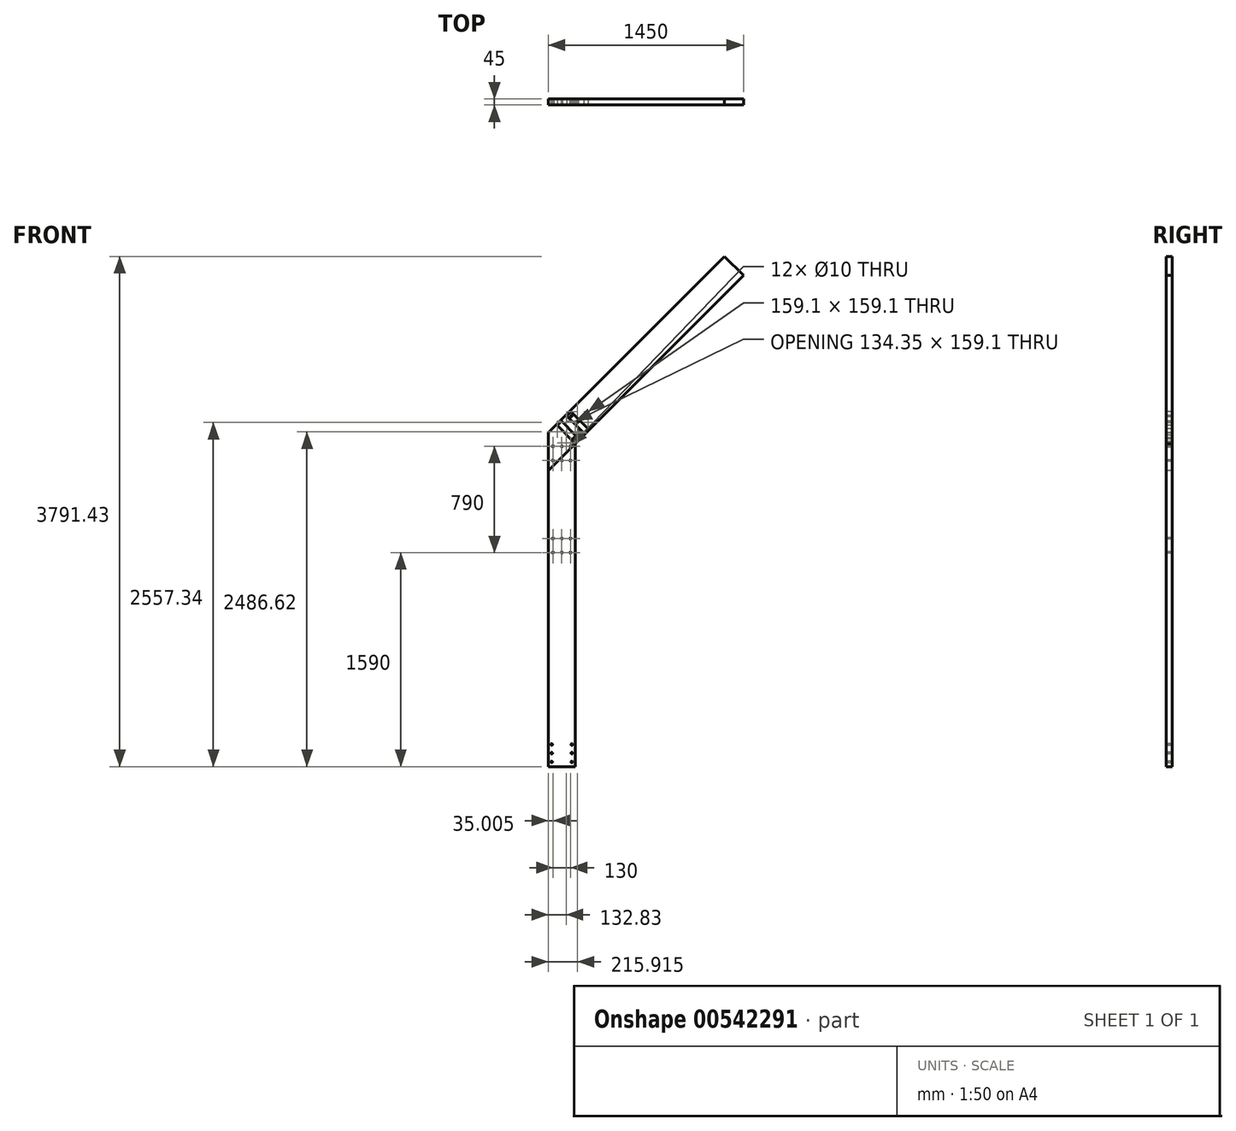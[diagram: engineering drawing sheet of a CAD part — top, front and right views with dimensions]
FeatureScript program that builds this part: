
annotation { "Feature Type Name" : "Feature", "Feature Type Description" : "" }
export const myFeature = defineFeature(function(context is Context, id is Id, definition is map)
    precondition{}
    {
        {
            var Q0;
            Q0=qCreatedBy(makeId("Front.planeOp"),FACE);
            var sketch = newSketch(context, id + "F0", { "sketchPlane" : qUnion([Q0])});
            skLineSegment(sketch, "E0.bottom", {"start": v(-2887.08, 383.58) * mm, "end": v(-5387.08, 383.58) * mm});
            skLineSegment(sketch, "E0.top", {"start": v(-2887.08, -1816.42) * mm, "end": v(-5387.08, -1816.42) * mm});
            skLineSegment(sketch, "E0.left", {"start": v(-2887.08, 383.58) * mm, "end": v(-2887.08, -1816.42) * mm});
            skLineSegment(sketch, "E0.right", {"start": v(-5387.08, 383.58) * mm, "end": v(-5387.08, -1816.42) * mm});
            skLineSegment(sketch, "E1", {"start": v(-5387.08, 383.58) * mm, "end": v(-4137.08, 1633.58) * mm});
            skPoint(sketch, "E1.endSnap0", {"position": v(-4137.08, 383.58) * mm});
            skLineSegment(sketch, "E2", {"start": v(-4137.08, 1633.58) * mm, "end": v(-2887.08, 383.58) * mm});
            skLineSegment(sketch, "E3.0", {"start": v(-4137.08, 1916.43) * mm, "end": v(-2687.08, 466.43) * mm});
            skLineSegment(sketch, "E3.1", {"start": v(-5587.08, 466.43) * mm, "end": v(-4137.08, 1916.43) * mm});
            skLineSegment(sketch, "E3.2", {"start": v(-2687.08, 466.43) * mm, "end": v(-2687.08, -2016.42) * mm});
            skLineSegment(sketch, "E3.3", {"start": v(-2687.08, -2016.42) * mm, "end": v(-5587.08, -2016.42) * mm});
            skLineSegment(sketch, "E3.4", {"start": v(-5587.08, 466.43) * mm, "end": v(-5587.08, -2016.42) * mm});
            skLineSegment(sketch, "E4", {"start": v(-5387.08, -1816.42) * mm, "end": v(-5587.08, -1816.42) * mm});
            skLineSegment(sketch, "E5", {"start": v(-5387.08, -1816.42) * mm, "end": v(-5387.08, -2016.42) * mm});
            skLineSegment(sketch, "E6", {"start": v(-5387.08, 383.58) * mm, "end": v(-5587.08, 466.43) * mm, "construction": true});
            skLineSegment(sketch, "E7", {"start": v(-5387.08, 383.58) * mm, "end": v(-5587.08, 183.58) * mm});
            skLineSegment(sketch, "E8", {"start": v(-5387.08, 383.58) * mm, "end": v(-5387.08, 666.43) * mm});
            skLineSegment(sketch, "E9", {"start": v(-4137.08, 1633.58) * mm, "end": v(-3995.65, 1775) * mm});
            skLineSegment(sketch, "E10", {"start": v(-4137.08, 1633.58) * mm, "end": v(-4278.5, 1775) * mm});
            skLineSegment(sketch, "E11", {"start": v(-5532.08, -2016.42) * mm, "end": v(-5532.08, -1816.42) * mm});
            skLineSegment(sketch, "E12", {"start": v(-5442.08, -1816.42) * mm, "end": v(-5442.08, -2016.42) * mm});
            skLineSegment(sketch, "E13", {"start": v(-2887.08, -1816.42) * mm, "end": v(-2687.08, -1816.42) * mm});
            skLineSegment(sketch, "E14", {"start": v(-2887.08, -1816.42) * mm, "end": v(-2887.08, -2016.42) * mm});
            skLineSegment(sketch, "E15", {"start": v(-2832.08, -1816.42) * mm, "end": v(-2832.08, -2016.42) * mm});
            skLineSegment(sketch, "E16", {"start": v(-2742.08, -1816.42) * mm, "end": v(-2742.08, -2016.42) * mm});
            skLineSegment(sketch, "E17", {"start": v(-4137.08, -1816.42) * mm, "end": v(-4137.08, -2016.42) * mm});
            skLineSegment(sketch, "E18", {"start": v(-4182.08, -1816.42) * mm, "end": v(-4182.08, -2016.42) * mm});
            skLineSegment(sketch, "E19", {"start": v(-4092.08, -1816.42) * mm, "end": v(-4092.08, -2016.42) * mm});
            skLineSegment(sketch, "E20", {"start": v(-4232.08, -1816.42) * mm, "end": v(-4232.08, -2016.42) * mm});
            skLineSegment(sketch, "E21", {"start": v(-4857.08, -1816.42) * mm, "end": v(-4857.08, -2016.42) * mm});
            skLineSegment(sketch, "E22", {"start": v(-4767.08, -1816.42) * mm, "end": v(-4767.08, -2016.42) * mm});
            skLineSegment(sketch, "E23", {"start": v(-4907.08, -1816.42) * mm, "end": v(-4907.08, -2016.42) * mm});
            skLineSegment(sketch, "E24", {"start": v(-4717.08, -1816.42) * mm, "end": v(-4717.08, -2016.42) * mm});
            skLineSegment(sketch, "E25.MirrorCS", {"start": v(-3557.08, -1816.42) * mm, "end": v(-3557.08, -2016.42) * mm});
            skLineSegment(sketch, "E26.MirrorCS", {"start": v(-3507.08, -1816.42) * mm, "end": v(-3507.08, -2016.42) * mm});
            skLineSegment(sketch, "E27.MirrorCS", {"start": v(-3417.08, -1816.42) * mm, "end": v(-3417.08, -2016.42) * mm});
            skLineSegment(sketch, "E28.MirrorCS", {"start": v(-3367.08, -1816.42) * mm, "end": v(-3367.08, -2016.42) * mm});
            skLineSegment(sketch, "E29", {"start": v(-5587.08, -1766.42) * mm, "end": v(-5387.08, -1766.42) * mm});
            skLineSegment(sketch, "E30", {"start": v(-5587.08, -1721.42) * mm, "end": v(-5387.08, -1721.42) * mm});
            skLineSegment(sketch, "E31", {"start": v(-5587.08, -1671.42) * mm, "end": v(-5387.08, -1671.42) * mm});
            skLineSegment(sketch, "E32", {"start": v(-5387.08, 333.58) * mm, "end": v(-5587.08, 333.58) * mm});
            skLineSegment(sketch, "E33", {"start": v(-5587.08, 288.58) * mm, "end": v(-5387.08, 288.58) * mm});
            skLineSegment(sketch, "E34", {"start": v(-5587.08, 238.58) * mm, "end": v(-5387.08, 238.58) * mm});
            skLineSegment(sketch, "E35", {"start": v(-5587.08, -1131.42) * mm, "end": v(-5387.08, -1131.42) * mm});
            skLineSegment(sketch, "E36", {"start": v(-5587.08, -1081.42) * mm, "end": v(-5387.08, -1081.42) * mm});
            skLineSegment(sketch, "E37", {"start": v(-5587.08, -1036.42) * mm, "end": v(-5387.08, -1036.42) * mm});
            skLineSegment(sketch, "E38", {"start": v(-5587.08, -986.42) * mm, "end": v(-5387.08, -986.42) * mm});
            skLineSegment(sketch, "E39", {"start": v(-5587.08, -446.42) * mm, "end": v(-5387.08, -446.42) * mm});
            skLineSegment(sketch, "E40", {"start": v(-5587.08, -396.42) * mm, "end": v(-5387.08, -396.42) * mm});
            skLineSegment(sketch, "E41", {"start": v(-5587.08, -351.42) * mm, "end": v(-5387.08, -351.42) * mm});
            skLineSegment(sketch, "E42", {"start": v(-5587.08, -301.42) * mm, "end": v(-5387.08, -301.42) * mm});
            skLineSegment(sketch, "E43", {"start": v(-5387.08, 383.58) * mm, "end": v(-5587.08, 383.58) * mm});
            skLineSegment(sketch, "E44", {"start": v(-5387.08, 383.58) * mm, "end": v(-5528.5, 525) * mm});
            skLineSegment(sketch, "E45", {"start": v(-5493.14, 560.36) * mm, "end": v(-5351.72, 418.94) * mm});
            skLineSegment(sketch, "E46", {"start": v(-5461.32, 592.18) * mm, "end": v(-5319.9, 450.76) * mm});
            skLineSegment(sketch, "E47", {"start": v(-5425.97, 627.54) * mm, "end": v(-5284.54, 486.11) * mm});
            skLineSegment(sketch, "E48", {"start": v(-4313.85, 1739.65) * mm, "end": v(-4172.43, 1598.23) * mm});
            skLineSegment(sketch, "E49", {"start": v(-4345.67, 1707.83) * mm, "end": v(-4204.25, 1566.4) * mm});
            skLineSegment(sketch, "E50", {"start": v(-4381.03, 1672.47) * mm, "end": v(-4239.6, 1531.05) * mm});
            skLineSegment(sketch, "E51", {"start": v(-4955.03, 1098.47) * mm, "end": v(-4813.61, 957.05) * mm});
            skLineSegment(sketch, "E52", {"start": v(-4919.68, 1133.82) * mm, "end": v(-4778.26, 992.4) * mm});
            skLineSegment(sketch, "E53", {"start": v(-4887.86, 1165.64) * mm, "end": v(-4746.44, 1024.22) * mm});
            skLineSegment(sketch, "E54", {"start": v(-4852.5, 1201) * mm, "end": v(-4711.08, 1059.58) * mm});
            skLineSegment(sketch, "E55", {"start": v(-2882.08, -1816.42) * mm, "end": v(-2882.08, -2016.42) * mm});
            skLineSegment(sketch, "E56", {"start": v(-2692.08, -1816.42) * mm, "end": v(-2692.08, -2016.42) * mm});
            skLineSegment(sketch, "E57", {"start": v(-5582.9, -1816.42) * mm, "end": v(-5582.9, -2016.42) * mm});
            skLineSegment(sketch, "E58", {"start": v(-5392.08, -1816.42) * mm, "end": v(-5392.08, -2016.42) * mm});
            skLineSegment(sketch, "E59.MirrorCS", {"start": v(-4042.08, -1816.42) * mm, "end": v(-4042.08, -2016.42) * mm});
            skLineSegment(sketch, "E60", {"start": v(-3507.08, -2016.42) * mm, "end": v(-3507.08, -2085.64) * mm});
            skLineSegment(sketch, "E61", {"start": v(-5487.08, -1816.42) * mm, "end": v(-5487.08, -2016.42) * mm});
            skLineSegment(sketch, "E62", {"start": v(-4812.08, -2016.42) * mm, "end": v(-4812.08, -1816.42) * mm});
            skLineSegment(sketch, "E63", {"start": v(-5587.08, 363.58) * mm, "end": v(-5387.08, 363.58) * mm, "construction": true});
            skLineSegment(sketch, "E64", {"start": v(-5587.08, 258.58) * mm, "end": v(-5387.08, 258.58) * mm, "construction": true});
            skLineSegment(sketch, "E65.MirrorCS", {"start": v(-5514.35, 539.15) * mm, "end": v(-5372.93, 397.73) * mm, "construction": true});
            skLineSegment(sketch, "E66.MirrorCS", {"start": v(-5440.1, 613.4) * mm, "end": v(-5298.69, 471.97) * mm, "construction": true});
            skCircle(sketch, "E67", {"center": v(-5552.08, 363.58) * mm, "radius": 5 * mm});
            skCircle(sketch, "E68", {"center": v(-5422.08, 363.58) * mm, "radius": 5 * mm});
            skCircle(sketch, "E69", {"center": v(-5487.08, 363.58) * mm, "radius": 5 * mm});
            skCircle(sketch, "E70", {"center": v(-5552.08, 258.58) * mm, "radius": 5 * mm});
            skCircle(sketch, "E71", {"center": v(-5487.08, 258.58) * mm, "radius": 5 * mm});
            skCircle(sketch, "E72", {"center": v(-5422.08, 258.58) * mm, "radius": 5 * mm});
            skLineSegment(sketch, "E73", {"start": v(-5577.08, 383.58) * mm, "end": v(-5577.08, 333.58) * mm});
            skLineSegment(sketch, "E74", {"start": v(-5577.08, 288.58) * mm, "end": v(-5577.08, 238.58) * mm});
            skLineSegment(sketch, "E75", {"start": v(-5397.08, 383.58) * mm, "end": v(-5397.08, 333.58) * mm});
            skLineSegment(sketch, "E76", {"start": v(-5397.08, 288.58) * mm, "end": v(-5397.08, 238.58) * mm});
            skLineSegment(sketch, "E77", {"start": v(-5577.08, 338.58) * mm, "end": v(-5397.08, 338.58) * mm});
            skLineSegment(sketch, "E78", {"start": v(-5577.08, 283.58) * mm, "end": v(-5397.08, 283.58) * mm});
            skPoint(sketch, "E79", {"position": v(-5519.58, 363.58) * mm});
            skLineSegment(sketch, "E80.MirrorCS", {"start": v(-5521.43, 517.93) * mm, "end": v(-5486.07, 553.29) * mm});
            skLineSegment(sketch, "E81.MirrorCS", {"start": v(-5394.15, 390.66) * mm, "end": v(-5358.8, 426.01) * mm});
            skLineSegment(sketch, "E82.MirrorCS", {"start": v(-5489.6, 549.75) * mm, "end": v(-5362.33, 422.47) * mm});
            skCircle(sketch, "E83.MirrorC", {"center": v(-5397.68, 422.47) * mm, "radius": 5 * mm});
            skCircle(sketch, "E84.MirrorC", {"center": v(-5443.64, 468.44) * mm, "radius": 5 * mm});
            skCircle(sketch, "E85.MirrorC", {"center": v(-5489.6, 514.4) * mm, "radius": 5 * mm});
            skLineSegment(sketch, "E86.MirrorCS", {"start": v(-5450.71, 588.65) * mm, "end": v(-5323.44, 461.37) * mm});
            skCircle(sketch, "E87.MirrorC", {"center": v(-5415.36, 588.65) * mm, "radius": 5 * mm});
            skCircle(sketch, "E88.MirrorC", {"center": v(-5369.4, 542.68) * mm, "radius": 5 * mm});
            skCircle(sketch, "E89.MirrorC", {"center": v(-5323.44, 496.72) * mm, "radius": 5 * mm});
            skLineSegment(sketch, "E90.MirrorCS", {"start": v(-5326.97, 457.83) * mm, "end": v(-5291.62, 493.19) * mm});
            skLineSegment(sketch, "E91.MirrorCS", {"start": v(-5454.25, 585.1) * mm, "end": v(-5418.9, 620.46) * mm});
            skLineSegment(sketch, "E92", {"start": v(-4310.32, 1743.19) * mm, "end": v(-4168.9, 1601.76) * mm});
            skLineSegment(sketch, "E93", {"start": v(-4349.2, 1704.3) * mm, "end": v(-4207.79, 1562.87) * mm});
            skLineSegment(sketch, "E94", {"start": v(-4925.33, 1128.17) * mm, "end": v(-4783.91, 986.75) * mm});
            skLineSegment(sketch, "E95", {"start": v(-4882.2, 1171.3) * mm, "end": v(-4740.78, 1029.88) * mm});
            skLineSegment(sketch, "E96", {"start": v(-5587.08, -346.42) * mm, "end": v(-5387.08, -346.42) * mm});
            skLineSegment(sketch, "E97", {"start": v(-5587.08, -401.42) * mm, "end": v(-5387.08, -401.42) * mm});
            skLineSegment(sketch, "E98", {"start": v(-5587.08, -1028.42) * mm, "end": v(-5387.08, -1028.42) * mm});
            skLineSegment(sketch, "E99", {"start": v(-5587.08, -1089.42) * mm, "end": v(-5387.08, -1089.42) * mm});
            skLineSegment(sketch, "E100", {"start": v(-5587.08, -1716.42) * mm, "end": v(-5387.08, -1716.42) * mm});
            skLineSegment(sketch, "E101", {"start": v(-5587.08, -1771.42) * mm, "end": v(-5387.08, -1771.42) * mm});
            skLineSegment(sketch, "E102", {"start": v(-5540.08, -1816.42) * mm, "end": v(-5540.08, -2016.42) * mm});
            skLineSegment(sketch, "E103", {"start": v(-5434.08, -1816.42) * mm, "end": v(-5434.08, -2016.42) * mm});
            skLineSegment(sketch, "E104", {"start": v(-4864.23, -1816.42) * mm, "end": v(-4864.23, -2016.42) * mm});
            skLineSegment(sketch, "E105", {"start": v(-4759.08, -1816.42) * mm, "end": v(-4759.08, -2016.42) * mm});
            skLineSegment(sketch, "E106", {"start": v(-4190.08, -1816.42) * mm, "end": v(-4190.08, -2016.42) * mm});
            skLineSegment(sketch, "E107", {"start": v(-5562.08, -1816.42) * mm, "end": v(-5562.08, -2016.42) * mm, "construction": true});
            skCircle(sketch, "E108", {"center": v(-5562.08, -1851.42) * mm, "radius": 6.17 * mm});
            skCircle(sketch, "E109", {"center": v(-5562.08, -1916.42) * mm, "radius": 6 * mm});
            skCircle(sketch, "E110", {"center": v(-5562.08, -1981.42) * mm, "radius": 6 * mm});
            skCircle(sketch, "E111.MirrorC", {"center": v(-5412.08, -1851.42) * mm, "radius": 6.17 * mm});
            skCircle(sketch, "E112.MirrorC", {"center": v(-5412.08, -1916.42) * mm, "radius": 6 * mm});
            skCircle(sketch, "E113.MirrorC", {"center": v(-5412.08, -1981.42) * mm, "radius": 6 * mm});
            skLineSegment(sketch, "E114", {"start": v(-4137.08, 1633.58) * mm, "end": v(-4137.08, 1916.43) * mm});
            skLineSegment(sketch, "E115.bottom", {"start": v(-5587.08, -2016.42) * mm, "end": v(-5645.08, -2016.42) * mm});
            skLineSegment(sketch, "E115.left", {"start": v(-5587.08, -2016.42) * mm, "end": v(-5587.08, -1971.42) * mm});
            skLineSegment(sketch, "E116.bottom", {"start": v(-5645.08, -2016.42) * mm, "end": v(-4137.08, -2016.42) * mm});
            skLineSegment(sketch, "E116.right", {"start": v(-4137.08, -2016.42) * mm, "end": v(-4137.08, -2029.42) * mm});
            skLineSegment(sketch, "E117", {"start": v(-5587.08, 466.43) * mm, "end": v(-5641.54, 488.99) * mm, "construction": true});
            skLineSegment(sketch, "E118", {"start": v(-5600.08, 471.81) * mm, "end": v(-5587.08, 466.43) * mm});
            skLineSegment(sketch, "E119", {"start": v(-4137.08, 1934.81) * mm, "end": v(-4137.08, 1916.43) * mm});
            skLineSegment(sketch, "E120", {"start": v(-4354.86, 1780.66) * mm, "end": v(-4137.08, 1998.45) * mm});
            skLineSegment(sketch, "E121", {"start": v(-4137.08, 1998.45) * mm, "end": v(-4137.08, 2030.98) * mm});
            skLineSegment(sketch, "E122", {"start": v(-4137.08, 1916.43) * mm, "end": v(-4137.08, 2145.54) * mm, "construction": true});
            skLineSegment(sketch, "E123", {"start": v(-5587.08, -321.42) * mm, "end": v(-5387.08, -321.42) * mm, "construction": true});
            skLineSegment(sketch, "E124", {"start": v(-5587.08, -426.42) * mm, "end": v(-5387.08, -426.42) * mm, "construction": true});
            skCircle(sketch, "E125", {"center": v(-5552.08, -321.42) * mm, "radius": 5 * mm});
            skCircle(sketch, "E126", {"center": v(-5487.08, -321.42) * mm, "radius": 5 * mm});
            skCircle(sketch, "E127", {"center": v(-5422.08, -321.42) * mm, "radius": 5 * mm});
            skLineSegment(sketch, "E128", {"start": v(-5587.08, -373.92) * mm, "end": v(-5387.08, -373.92) * mm, "construction": true});
            skCircle(sketch, "E129.MirrorC", {"center": v(-5552.08, -426.42) * mm, "radius": 5 * mm});
            skCircle(sketch, "E130.MirrorC", {"center": v(-5487.08, -426.42) * mm, "radius": 5 * mm});
            skCircle(sketch, "E131.MirrorC", {"center": v(-5422.08, -426.42) * mm, "radius": 5 * mm});
            skLineSegment(sketch, "E132", {"start": v(-2887.08, 383.58) * mm, "end": v(-2687.08, 183.58) * mm});
            skLineSegment(sketch, "E133", {"start": v(-2887.08, 383.58) * mm, "end": v(-2887.08, 666.43) * mm});
            skSolve(sketch);
        }
        {
            var Q0;
            {var subQ0=sQuery(id+"F0.wireOp",EDGE,"E31");Q0=makeQuery(id+"F0.imprint","IMPRINT",FACE,{"disambiguationData":[TD([[makeQuery(id+"F0.imprint","IMPRINT",EDGE,{"derivedFrom":subQ0}),1.0]])]});}
            var Q1;
            {var subQ0=sQuery(id+"F0.wireOp",EDGE,"E31");Q1=makeQuery(id+"F0.imprint","IMPRINT",FACE,{"disambiguationData":[TD([[makeQuery(id+"F0.imprint","IMPRINT",EDGE,{"derivedFrom":subQ0}),-1.0]])]});}
            var Q2;
            {var subQ0=sQuery(id+"F0.wireOp",EDGE,"E30");Q2=makeQuery(id+"F0.imprint","IMPRINT",FACE,{"disambiguationData":[TD([[makeQuery(id+"F0.imprint","IMPRINT",EDGE,{"derivedFrom":subQ0}),1.0]])]});}
            var Q3;
            {var subQ0=sQuery(id+"F0.wireOp",EDGE,"E29");Q3=makeQuery(id+"F0.imprint","IMPRINT",FACE,{"disambiguationData":[TD([[makeQuery(id+"F0.imprint","IMPRINT",EDGE,{"derivedFrom":subQ0}),1.0]])]});}
            var Q4;
            {var subQ0=sQuery(id+"F0.wireOp",EDGE,"E29");Q4=makeQuery(id+"F0.imprint","IMPRINT",FACE,{"disambiguationData":[TD([[makeQuery(id+"F0.imprint","IMPRINT",EDGE,{"derivedFrom":subQ0}),-1.0]])]});}
            var Q5;
            {var subQ11=sQuery(id+"F0.wireOp",EDGE,"E101");Q5=makeQuery(id+"F0.imprint","IMPRINT",FACE,{"disambiguationData":[TD([[makeQuery(id+"F0.imprint","IMPRINT",EDGE,{"derivedFrom":subQ11}),-1.0]])]});}
            var Q6;
            {var subQ0=sQuery(id+"F0.wireOp",EDGE,"E11");Q6=makeQuery(id+"F0.imprint","IMPRINT",FACE,{"disambiguationData":[TD([[makeQuery(id+"F0.imprint","IMPRINT",EDGE,{"derivedFrom":subQ0}),-1.0]])]});}
            var Q7;
            {var subQ1=sQuery(id+"F0.wireOp",EDGE,"E57");Q7=makeQuery(id+"F0.imprint","IMPRINT",FACE,{"disambiguationData":[TD([[makeQuery(id+"F0.imprint","IMPRINT",EDGE,{"derivedFrom":subQ1}),1.0]])]});}
            var Q8;
            {var subQ0=sQuery(id+"F0.wireOp",EDGE,"E11");Q8=makeQuery(id+"F0.imprint","IMPRINT",FACE,{"disambiguationData":[TD([[makeQuery(id+"F0.imprint","IMPRINT",EDGE,{"derivedFrom":subQ0}),1.0]])]});}
            var Q9;
            {var subQ1=sQuery(id+"F0.wireOp",EDGE,"E57");Q9=makeQuery(id+"F0.imprint","IMPRINT",FACE,{"disambiguationData":[TD([[makeQuery(id+"F0.imprint","IMPRINT",EDGE,{"derivedFrom":subQ1}),-1.0]])]});}
            var Q10;
            {var subQ0=sQuery(id+"F0.wireOp",EDGE,"E12");Q10=makeQuery(id+"F0.imprint","IMPRINT",FACE,{"disambiguationData":[TD([[makeQuery(id+"F0.imprint","IMPRINT",EDGE,{"derivedFrom":subQ0}),-1.0]])]});}
            var Q11;
            {var subQ0=sQuery(id+"F0.wireOp",EDGE,"E12");Q11=makeQuery(id+"F0.imprint","IMPRINT",FACE,{"disambiguationData":[TD([[makeQuery(id+"F0.imprint","IMPRINT",EDGE,{"derivedFrom":subQ0}),1.0]])]});}
            var Q12;
            {var subQ1=sQuery(id+"F0.wireOp",EDGE,"E58");Q12=makeQuery(id+"F0.imprint","IMPRINT",FACE,{"disambiguationData":[TD([[makeQuery(id+"F0.imprint","IMPRINT",EDGE,{"derivedFrom":subQ1}),-1.0]])]});}
            var Q13;
            {var subQ0=sQuery(id+"F0.wireOp",EDGE,"E5");Q13=makeQuery(id+"F0.imprint","IMPRINT",FACE,{"disambiguationData":[TD([[makeQuery(id+"F0.imprint","IMPRINT",EDGE,{"derivedFrom":subQ0}),-1.0]])]});}
            var Q14;
            {var subQ0=sQuery(id+"F0.wireOp",EDGE,"E35");Q14=makeQuery(id+"F0.imprint","IMPRINT",FACE,{"disambiguationData":[TD([[makeQuery(id+"F0.imprint","IMPRINT",EDGE,{"derivedFrom":subQ0}),1.0]])]});}
            var Q15;
            {var subQ0=sQuery(id+"F0.wireOp",EDGE,"E36");Q15=makeQuery(id+"F0.imprint","IMPRINT",FACE,{"disambiguationData":[TD([[makeQuery(id+"F0.imprint","IMPRINT",EDGE,{"derivedFrom":subQ0}),-1.0]])]});}
            var Q16;
            {var subQ0=sQuery(id+"F0.wireOp",EDGE,"E36");Q16=makeQuery(id+"F0.imprint","IMPRINT",FACE,{"disambiguationData":[TD([[makeQuery(id+"F0.imprint","IMPRINT",EDGE,{"derivedFrom":subQ0}),1.0]])]});}
            var Q17;
            {var subQ0=sQuery(id+"F0.wireOp",EDGE,"E37");Q17=makeQuery(id+"F0.imprint","IMPRINT",FACE,{"disambiguationData":[TD([[makeQuery(id+"F0.imprint","IMPRINT",EDGE,{"derivedFrom":subQ0}),1.0]])]});}
            var Q18;
            {var subQ0=sQuery(id+"F0.wireOp",EDGE,"E38");Q18=makeQuery(id+"F0.imprint","IMPRINT",FACE,{"disambiguationData":[TD([[makeQuery(id+"F0.imprint","IMPRINT",EDGE,{"derivedFrom":subQ0}),-1.0]])]});}
            var Q19;
            {var subQ0=sQuery(id+"F0.wireOp",EDGE,"E38");Q19=makeQuery(id+"F0.imprint","IMPRINT",FACE,{"disambiguationData":[TD([[makeQuery(id+"F0.imprint","IMPRINT",EDGE,{"derivedFrom":subQ0}),1.0]])]});}
            var Q20;
            {var subQ1=sQuery(id+"F0.wireOp",EDGE,"E39");Q20=makeQuery(id+"F0.imprint","IMPRINT",FACE,{"disambiguationData":[TD([[makeQuery(id+"F0.imprint","IMPRINT",EDGE,{"derivedFrom":subQ1}),1.0]])]});}
            var Q21;
            {var subQ0=sQuery(id+"F0.wireOp",EDGE,"E40");Q21=makeQuery(id+"F0.imprint","IMPRINT",FACE,{"disambiguationData":[TD([[makeQuery(id+"F0.imprint","IMPRINT",EDGE,{"derivedFrom":subQ0}),-1.0]])]});}
            var Q22;
            {var subQ0=sQuery(id+"F0.wireOp",EDGE,"E40");Q22=makeQuery(id+"F0.imprint","IMPRINT",FACE,{"disambiguationData":[TD([[makeQuery(id+"F0.imprint","IMPRINT",EDGE,{"derivedFrom":subQ0}),1.0]])]});}
            var Q23;
            {var subQ0=sQuery(id+"F0.wireOp",EDGE,"E41");Q23=makeQuery(id+"F0.imprint","IMPRINT",FACE,{"disambiguationData":[TD([[makeQuery(id+"F0.imprint","IMPRINT",EDGE,{"derivedFrom":subQ0}),1.0]])]});}
            var Q24;
            {var subQ0=sQuery(id+"F0.wireOp",EDGE,"E42");Q24=makeQuery(id+"F0.imprint","IMPRINT",FACE,{"disambiguationData":[TD([[makeQuery(id+"F0.imprint","IMPRINT",EDGE,{"derivedFrom":subQ0}),-1.0]])]});}
            var Q25;
            {var subQ6=sQuery(id+"F0.wireOp",EDGE,"E42");Q25=makeQuery(id+"F0.imprint","IMPRINT",FACE,{"disambiguationData":[TD([[makeQuery(id+"F0.imprint","IMPRINT",EDGE,{"derivedFrom":subQ6}),1.0]])]});}
            var Q26;
            {var subQ0=sQuery(id+"F0.wireOp",EDGE,"E32");var subQ1=sQuery(id+"F0.wireOp",EDGE,"E0.right");var subQ2=makeQuery(id+"F0.imprint","INTERSECT",VERTEX,{"derivedFrom":[subQ1,subQ0]});Q26=makeQuery(id+"F0.imprint","IMPRINT",FACE,{"disambiguationData":[TD([[makeQuery(id+"F0.imprint","IMPRINT",EDGE,{"disambiguationData":[TD([[subQ2,-1.0]])],"derivedFrom":subQ1}),-1.0]])]});}
            var Q27;
            Q27=makeQuery(id+"F0.imprint","IMPRINT",FACE,{"disambiguationData":[TD([[makeQuery(id+"F0.imprint","IMPRINT",EDGE,{"derivedFrom":sQuery(id+"F0.wireOp",EDGE,"E71")}),-1.0]])]});
            var Q28;
            {var subQ1=sQuery(id+"F0.wireOp",EDGE,"E33");var subQ5=sQuery(id+"F0.wireOp",EDGE,"E0.right");var subQ8=makeQuery(id+"F0.imprint","INTERSECT",VERTEX,{"derivedFrom":[subQ5,subQ1]});Q28=makeQuery(id+"F0.imprint","IMPRINT",FACE,{"disambiguationData":[TD([[makeQuery(id+"F0.imprint","IMPRINT",EDGE,{"disambiguationData":[TD([[subQ8,-1.0]])],"derivedFrom":subQ5}),-1.0]])]});}
            var Q29;
            {var subQ0=sQuery(id+"F0.wireOp",EDGE,"E33");var subQ1=sQuery(id+"F0.wireOp",EDGE,"E7");var subQ2=makeQuery(id+"F0.imprint","INTERSECT",VERTEX,{"derivedFrom":[subQ1,subQ0]});Q29=makeQuery(id+"F0.imprint","IMPRINT",FACE,{"disambiguationData":[TD([[makeQuery(id+"F0.imprint","IMPRINT",EDGE,{"disambiguationData":[TD([[subQ2,-1.0]])],"derivedFrom":subQ1}),1.0]])]});}
            var Q30;
            {var subQ0=sQuery(id+"F0.wireOp",EDGE,"E75");var subQ1=sQuery(id+"F0.wireOp",EDGE,"E7");var subQ2=makeQuery(id+"F0.imprint","INTERSECT",VERTEX,{"derivedFrom":[subQ1,subQ0]});Q30=makeQuery(id+"F0.imprint","IMPRINT",FACE,{"disambiguationData":[TD([[makeQuery(id+"F0.imprint","IMPRINT",EDGE,{"disambiguationData":[TD([[subQ2,-1.0]])],"derivedFrom":subQ1}),1.0]])]});}
            var Q31;
            {var subQ0=sQuery(id+"F0.wireOp",EDGE,"E77");var subQ1=sQuery(id+"F0.wireOp",EDGE,"E7");var subQ2=makeQuery(id+"F0.imprint","INTERSECT",VERTEX,{"derivedFrom":[subQ1,subQ0]});Q31=makeQuery(id+"F0.imprint","IMPRINT",FACE,{"disambiguationData":[TD([[makeQuery(id+"F0.imprint","IMPRINT",EDGE,{"disambiguationData":[TD([[subQ2,-1.0]])],"derivedFrom":subQ1}),1.0]])]});}
            var Q32;
            {var subQ4=sQuery(id+"F0.wireOp",EDGE,"E0.right");var subQ6=sQuery(id+"F0.wireOp",EDGE,"E32");var subQ7=makeQuery(id+"F0.imprint","INTERSECT",VERTEX,{"derivedFrom":[subQ4,subQ6]});Q32=makeQuery(id+"F0.imprint","IMPRINT",FACE,{"disambiguationData":[TD([[makeQuery(id+"F0.imprint","IMPRINT",EDGE,{"disambiguationData":[TD([[subQ7,-1.0]])],"derivedFrom":subQ6}),-1.0]])]});}
            extrude(context, id + "F1", {"entities" : qUnion([Q0, Q1, Q2, Q3, Q4, Q5, Q6, Q7, Q8, Q9, Q10, Q11, Q12, Q13, Q14, Q15, Q16, Q17, Q18, Q19, Q20, Q21, Q22, Q23, Q24, Q25, Q26, Q27, Q28, Q29, Q30, Q31, Q32]), "depth" : -45 * mm, "offsetDistance" : 25 * mm});
        }
        {
            var Q0;
            {var subQ0=sQuery(id+"F0.wireOp",EDGE,"E7");var subQ1=sQuery(id+"F0.wireOp",EDGE,"E3.4");var subQ2=makeQuery(id+"F0.imprint","INTERSECT",VERTEX,{"derivedFrom":[subQ1,subQ0]});Q0=makeQuery(id+"F0.imprint","IMPRINT",FACE,{"disambiguationData":[TD([[makeQuery(id+"F0.imprint","IMPRINT",EDGE,{"disambiguationData":[TD([[subQ2,1.0]])],"derivedFrom":subQ1}),1.0]])]});}
            var Q1;
            Q1=makeQuery(id+"F0.imprint","IMPRINT",FACE,{"disambiguationData":[TD([[makeQuery(id+"F0.imprint","IMPRINT",EDGE,{"derivedFrom":sQuery(id+"F0.wireOp",EDGE,"E70")}),-1.0]])]});
            var Q2;
            {var subQ1=sQuery(id+"F0.wireOp",EDGE,"E33");var subQ5=sQuery(id+"F0.wireOp",EDGE,"E3.4");var subQ8=makeQuery(id+"F0.imprint","INTERSECT",VERTEX,{"derivedFrom":[subQ5,subQ1]});Q2=makeQuery(id+"F0.imprint","IMPRINT",FACE,{"disambiguationData":[TD([[makeQuery(id+"F0.imprint","IMPRINT",EDGE,{"disambiguationData":[TD([[subQ8,-1.0]])],"derivedFrom":subQ5}),1.0]])]});}
            var Q3;
            {var subQ0=sQuery(id+"F0.wireOp",EDGE,"E33");var subQ1=sQuery(id+"F0.wireOp",EDGE,"E7");var subQ2=makeQuery(id+"F0.imprint","INTERSECT",VERTEX,{"derivedFrom":[subQ1,subQ0]});Q3=makeQuery(id+"F0.imprint","IMPRINT",FACE,{"disambiguationData":[TD([[makeQuery(id+"F0.imprint","IMPRINT",EDGE,{"disambiguationData":[TD([[subQ2,-1.0]])],"derivedFrom":subQ1}),-1.0]])]});}
            var Q4;
            {var subQ0=sQuery(id+"F0.wireOp",EDGE,"E32");var subQ6=sQuery(id+"F0.wireOp",EDGE,"E3.4");var subQ7=makeQuery(id+"F0.imprint","INTERSECT",VERTEX,{"derivedFrom":[subQ6,subQ0]});Q4=makeQuery(id+"F0.imprint","IMPRINT",FACE,{"disambiguationData":[TD([[makeQuery(id+"F0.imprint","IMPRINT",EDGE,{"disambiguationData":[TD([[subQ7,-1.0]])],"derivedFrom":subQ6}),1.0]])]});}
            var Q5;
            {var subQ0=sQuery(id+"F0.wireOp",EDGE,"E77");var subQ1=sQuery(id+"F0.wireOp",EDGE,"E7");var subQ2=makeQuery(id+"F0.imprint","INTERSECT",VERTEX,{"derivedFrom":[subQ1,subQ0]});Q5=makeQuery(id+"F0.imprint","IMPRINT",FACE,{"disambiguationData":[TD([[makeQuery(id+"F0.imprint","IMPRINT",EDGE,{"disambiguationData":[TD([[subQ2,-1.0]])],"derivedFrom":subQ1}),-1.0]])]});}
            var Q6;
            Q6=makeQuery(id+"F0.imprint","IMPRINT",FACE,{"disambiguationData":[TD([[makeQuery(id+"F0.imprint","IMPRINT",EDGE,{"derivedFrom":sQuery(id+"F0.wireOp",EDGE,"E67")}),-1.0]])]});
            var Q7;
            {var subQ4=sQuery(id+"F0.wireOp",EDGE,"E32");var subQ5=sQuery(id+"F0.wireOp",EDGE,"E3.4");var subQ6=makeQuery(id+"F0.imprint","INTERSECT",VERTEX,{"derivedFrom":[subQ5,subQ4]});Q7=makeQuery(id+"F0.imprint","IMPRINT",FACE,{"disambiguationData":[TD([[makeQuery(id+"F0.imprint","IMPRINT",EDGE,{"disambiguationData":[TD([[subQ6,1.0]])],"derivedFrom":subQ5}),1.0]])]});}
            var Q8;
            {var subQ5=sQuery(id+"F0.wireOp",EDGE,"E3.4");var subQ6=sQuery(id+"F0.wireOp",EDGE,"E3.1");var subQ7=makeQuery(id+"F0.imprint","INTERSECT",VERTEX,{"derivedFrom":[subQ6,subQ5]});Q8=makeQuery(id+"F0.imprint","IMPRINT",FACE,{"disambiguationData":[TD([[makeQuery(id+"F0.imprint","IMPRINT",EDGE,{"disambiguationData":[TD([[subQ7,-1.0]])],"derivedFrom":subQ6}),-1.0]])]});}
            var Q9;
            Q9=makeQuery(id+"F0.imprint","IMPRINT",FACE,{"disambiguationData":[TD([[makeQuery(id+"F0.imprint","IMPRINT",EDGE,{"derivedFrom":sQuery(id+"F0.wireOp",EDGE,"E83.MirrorC")}),1.0]])]});
            var Q10;
            {var subQ0=sQuery(id+"F0.wireOp",EDGE,"E81.MirrorCS");var subQ1=sQuery(id+"F0.wireOp",EDGE,"E8");var subQ2=makeQuery(id+"F0.imprint","INTERSECT",VERTEX,{"derivedFrom":[subQ1,subQ0]});Q10=makeQuery(id+"F0.imprint","IMPRINT",FACE,{"disambiguationData":[TD([[makeQuery(id+"F0.imprint","IMPRINT",EDGE,{"disambiguationData":[TD([[subQ2,-1.0]])],"derivedFrom":subQ1}),-1.0]])]});}
            var Q11;
            {var subQ1=sQuery(id+"F0.wireOp",EDGE,"E1");var subQ6=sQuery(id+"F0.wireOp",EDGE,"E45");var subQ7=makeQuery(id+"F0.imprint","INTERSECT",VERTEX,{"derivedFrom":[subQ1,subQ6]});Q11=makeQuery(id+"F0.imprint","IMPRINT",FACE,{"disambiguationData":[TD([[makeQuery(id+"F0.imprint","IMPRINT",EDGE,{"disambiguationData":[TD([[subQ7,1.0]])],"derivedFrom":subQ6}),-1.0]])]});}
            var Q12;
            {var subQ0=sQuery(id+"F0.wireOp",EDGE,"E44");var subQ3=sQuery(id+"F0.wireOp",EDGE,"E81.MirrorCS");var subQ5=makeQuery(id+"F0.imprint","INTERSECT",VERTEX,{"derivedFrom":[subQ0,subQ3]});Q12=makeQuery(id+"F0.imprint","IMPRINT",FACE,{"disambiguationData":[TD([[makeQuery(id+"F0.imprint","IMPRINT",EDGE,{"disambiguationData":[TD([[subQ5,-1.0]])],"derivedFrom":subQ3}),-1.0]])]});}
            var Q13;
            {var subQ0=sQuery(id+"F0.wireOp",EDGE,"E43");var subQ3=sQuery(id+"F0.wireOp",EDGE,"E75");var subQ5=makeQuery(id+"F0.imprint","INTERSECT",VERTEX,{"derivedFrom":[subQ0,subQ3]});Q13=makeQuery(id+"F0.imprint","IMPRINT",FACE,{"disambiguationData":[TD([[makeQuery(id+"F0.imprint","IMPRINT",EDGE,{"disambiguationData":[TD([[subQ5,-1.0]])],"derivedFrom":subQ3}),1.0]])]});}
            var Q14;
            {var subQ1=sQuery(id+"F0.wireOp",EDGE,"E44");var subQ5=sQuery(id+"F0.wireOp",EDGE,"E3.1");var subQ8=makeQuery(id+"F0.imprint","INTERSECT",VERTEX,{"derivedFrom":[subQ5,subQ1]});Q14=makeQuery(id+"F0.imprint","IMPRINT",FACE,{"disambiguationData":[TD([[makeQuery(id+"F0.imprint","IMPRINT",EDGE,{"disambiguationData":[TD([[subQ8,-1.0]])],"derivedFrom":subQ5}),-1.0]])]});}
            var Q15;
            {var subQ0=sQuery(id+"F0.wireOp",EDGE,"E82.MirrorCS");var subQ1=sQuery(id+"F0.wireOp",EDGE,"E8");var subQ2=makeQuery(id+"F0.imprint","INTERSECT",VERTEX,{"derivedFrom":[subQ1,subQ0]});Q15=makeQuery(id+"F0.imprint","IMPRINT",FACE,{"disambiguationData":[TD([[makeQuery(id+"F0.imprint","IMPRINT",EDGE,{"disambiguationData":[TD([[subQ2,-1.0]])],"derivedFrom":subQ1}),1.0]])]});}
            var Q16;
            {var subQ0=sQuery(id+"F0.wireOp",EDGE,"E45");var subQ4=sQuery(id+"F0.wireOp",EDGE,"E3.1");var subQ5=makeQuery(id+"F0.imprint","INTERSECT",VERTEX,{"derivedFrom":[subQ4,subQ0]});Q16=makeQuery(id+"F0.imprint","IMPRINT",FACE,{"disambiguationData":[TD([[makeQuery(id+"F0.imprint","IMPRINT",EDGE,{"disambiguationData":[TD([[subQ5,-1.0]])],"derivedFrom":subQ4}),-1.0]])]});}
            var Q17;
            {var subQ0=sQuery(id+"F0.wireOp",EDGE,"E45");var subQ4=sQuery(id+"F0.wireOp",EDGE,"E1");var subQ5=makeQuery(id+"F0.imprint","INTERSECT",VERTEX,{"derivedFrom":[subQ4,subQ0]});Q17=makeQuery(id+"F0.imprint","IMPRINT",FACE,{"disambiguationData":[TD([[makeQuery(id+"F0.imprint","IMPRINT",EDGE,{"disambiguationData":[TD([[subQ5,-1.0]])],"derivedFrom":subQ4}),1.0]])]});}
            var Q18;
            {var subQ0=sQuery(id+"F0.wireOp",EDGE,"E82.MirrorCS");var subQ1=sQuery(id+"F0.wireOp",EDGE,"E8");var subQ2=makeQuery(id+"F0.imprint","INTERSECT",VERTEX,{"derivedFrom":[subQ1,subQ0]});Q18=makeQuery(id+"F0.imprint","IMPRINT",FACE,{"disambiguationData":[TD([[makeQuery(id+"F0.imprint","IMPRINT",EDGE,{"disambiguationData":[TD([[subQ2,-1.0]])],"derivedFrom":subQ1}),-1.0]])]});}
            var Q19;
            {var subQ0=sQuery(id+"F0.wireOp",EDGE,"E46");var subQ1=sQuery(id+"F0.wireOp",EDGE,"E8");var subQ2=makeQuery(id+"F0.imprint","INTERSECT",VERTEX,{"derivedFrom":[subQ1,subQ0]});Q19=makeQuery(id+"F0.imprint","IMPRINT",FACE,{"disambiguationData":[TD([[makeQuery(id+"F0.imprint","IMPRINT",EDGE,{"disambiguationData":[TD([[subQ2,-1.0]])],"derivedFrom":subQ1}),-1.0]])]});}
            var Q20;
            {var subQ1=sQuery(id+"F0.wireOp",EDGE,"E1");var subQ5=sQuery(id+"F0.wireOp",EDGE,"E46");var subQ6=makeQuery(id+"F0.imprint","INTERSECT",VERTEX,{"derivedFrom":[subQ1,subQ5]});Q20=makeQuery(id+"F0.imprint","IMPRINT",FACE,{"disambiguationData":[TD([[makeQuery(id+"F0.imprint","IMPRINT",EDGE,{"disambiguationData":[TD([[subQ6,-1.0]])],"derivedFrom":subQ1}),1.0]])]});}
            var Q21;
            Q21=makeQuery(id+"F0.imprint","IMPRINT",FACE,{"disambiguationData":[TD([[makeQuery(id+"F0.imprint","IMPRINT",EDGE,{"derivedFrom":sQuery(id+"F0.wireOp",EDGE,"E88.MirrorC")}),1.0]])]});
            var Q22;
            Q22=makeQuery(id+"F0.imprint","IMPRINT",FACE,{"disambiguationData":[TD([[makeQuery(id+"F0.imprint","IMPRINT",EDGE,{"derivedFrom":sQuery(id+"F0.wireOp",EDGE,"E87.MirrorC")}),1.0]])]});
            var Q23;
            {var subQ0=sQuery(id+"F0.wireOp",EDGE,"E46");var subQ1=sQuery(id+"F0.wireOp",EDGE,"E8");var subQ2=makeQuery(id+"F0.imprint","INTERSECT",VERTEX,{"derivedFrom":[subQ1,subQ0]});Q23=makeQuery(id+"F0.imprint","IMPRINT",FACE,{"disambiguationData":[TD([[makeQuery(id+"F0.imprint","IMPRINT",EDGE,{"disambiguationData":[TD([[subQ2,-1.0]])],"derivedFrom":subQ1}),1.0]])]});}
            var Q24;
            {var subQ2=sQuery(id+"F0.wireOp",EDGE,"E46");var subQ5=sQuery(id+"F0.wireOp",EDGE,"E3.1");var subQ8=makeQuery(id+"F0.imprint","INTERSECT",VERTEX,{"derivedFrom":[subQ5,subQ2]});Q24=makeQuery(id+"F0.imprint","IMPRINT",FACE,{"disambiguationData":[TD([[makeQuery(id+"F0.imprint","IMPRINT",EDGE,{"disambiguationData":[TD([[subQ8,-1.0]])],"derivedFrom":subQ5}),-1.0]])]});}
            var Q25;
            {var subQ0=sQuery(id+"F0.wireOp",EDGE,"E8");var subQ1=sQuery(id+"F0.wireOp",EDGE,"E3.1");var subQ2=makeQuery(id+"F0.imprint","INTERSECT",VERTEX,{"derivedFrom":[subQ1,subQ0]});Q25=makeQuery(id+"F0.imprint","IMPRINT",FACE,{"disambiguationData":[TD([[makeQuery(id+"F0.imprint","IMPRINT",EDGE,{"disambiguationData":[TD([[subQ2,1.0]])],"derivedFrom":subQ1}),-1.0]])]});}
            var Q26;
            {var subQ6=sQuery(id+"F0.wireOp",EDGE,"E51");Q26=makeQuery(id+"F0.imprint","IMPRINT",FACE,{"disambiguationData":[TD([[makeQuery(id+"F0.imprint","IMPRINT",EDGE,{"derivedFrom":subQ6}),-1.0]])]});}
            var Q27;
            {var subQ0=sQuery(id+"F0.wireOp",EDGE,"E51");Q27=makeQuery(id+"F0.imprint","IMPRINT",FACE,{"disambiguationData":[TD([[makeQuery(id+"F0.imprint","IMPRINT",EDGE,{"derivedFrom":subQ0}),1.0]])]});}
            var Q28;
            {var subQ0=sQuery(id+"F0.wireOp",EDGE,"E52");Q28=makeQuery(id+"F0.imprint","IMPRINT",FACE,{"disambiguationData":[TD([[makeQuery(id+"F0.imprint","IMPRINT",EDGE,{"derivedFrom":subQ0}),-1.0]])]});}
            var Q29;
            {var subQ0=sQuery(id+"F0.wireOp",EDGE,"E52");Q29=makeQuery(id+"F0.imprint","IMPRINT",FACE,{"disambiguationData":[TD([[makeQuery(id+"F0.imprint","IMPRINT",EDGE,{"derivedFrom":subQ0}),1.0]])]});}
            var Q30;
            {var subQ0=sQuery(id+"F0.wireOp",EDGE,"E53");Q30=makeQuery(id+"F0.imprint","IMPRINT",FACE,{"disambiguationData":[TD([[makeQuery(id+"F0.imprint","IMPRINT",EDGE,{"derivedFrom":subQ0}),1.0]])]});}
            var Q31;
            {var subQ0=sQuery(id+"F0.wireOp",EDGE,"E54");Q31=makeQuery(id+"F0.imprint","IMPRINT",FACE,{"disambiguationData":[TD([[makeQuery(id+"F0.imprint","IMPRINT",EDGE,{"derivedFrom":subQ0}),-1.0]])]});}
            var Q32;
            {var subQ0=sQuery(id+"F0.wireOp",EDGE,"E50");Q32=makeQuery(id+"F0.imprint","IMPRINT",FACE,{"disambiguationData":[TD([[makeQuery(id+"F0.imprint","IMPRINT",EDGE,{"derivedFrom":subQ0}),-1.0]])]});}
            var Q33;
            {var subQ0=sQuery(id+"F0.wireOp",EDGE,"E50");Q33=makeQuery(id+"F0.imprint","IMPRINT",FACE,{"disambiguationData":[TD([[makeQuery(id+"F0.imprint","IMPRINT",EDGE,{"derivedFrom":subQ0}),1.0]])]});}
            var Q34;
            {var subQ0=sQuery(id+"F0.wireOp",EDGE,"E49");Q34=makeQuery(id+"F0.imprint","IMPRINT",FACE,{"disambiguationData":[TD([[makeQuery(id+"F0.imprint","IMPRINT",EDGE,{"derivedFrom":subQ0}),-1.0]])]});}
            var Q35;
            {var subQ0=sQuery(id+"F0.wireOp",EDGE,"E48");Q35=makeQuery(id+"F0.imprint","IMPRINT",FACE,{"disambiguationData":[TD([[makeQuery(id+"F0.imprint","IMPRINT",EDGE,{"derivedFrom":subQ0}),-1.0]])]});}
            var Q36;
            {var subQ0=sQuery(id+"F0.wireOp",EDGE,"E48");Q36=makeQuery(id+"F0.imprint","IMPRINT",FACE,{"disambiguationData":[TD([[makeQuery(id+"F0.imprint","IMPRINT",EDGE,{"derivedFrom":subQ0}),1.0]])]});}
            var Q37;
            {var subQ0=sQuery(id+"F0.wireOp",EDGE,"E10");Q37=makeQuery(id+"F0.imprint","IMPRINT",FACE,{"disambiguationData":[TD([[makeQuery(id+"F0.imprint","IMPRINT",EDGE,{"derivedFrom":subQ0}),1.0]])]});}
            extrude(context, id + "F2", {"entities" : qUnion([Q0, Q1, Q2, Q3, Q4, Q5, Q6, Q7, Q8, Q9, Q10, Q11, Q12, Q13, Q14, Q15, Q16, Q17, Q18, Q19, Q20, Q21, Q22, Q23, Q24, Q25, Q26, Q27, Q28, Q29, Q30, Q31, Q32, Q33, Q34, Q35, Q36, Q37]), "depth" : -45 * mm, "offsetDistance" : 25 * mm});
        }
    });
